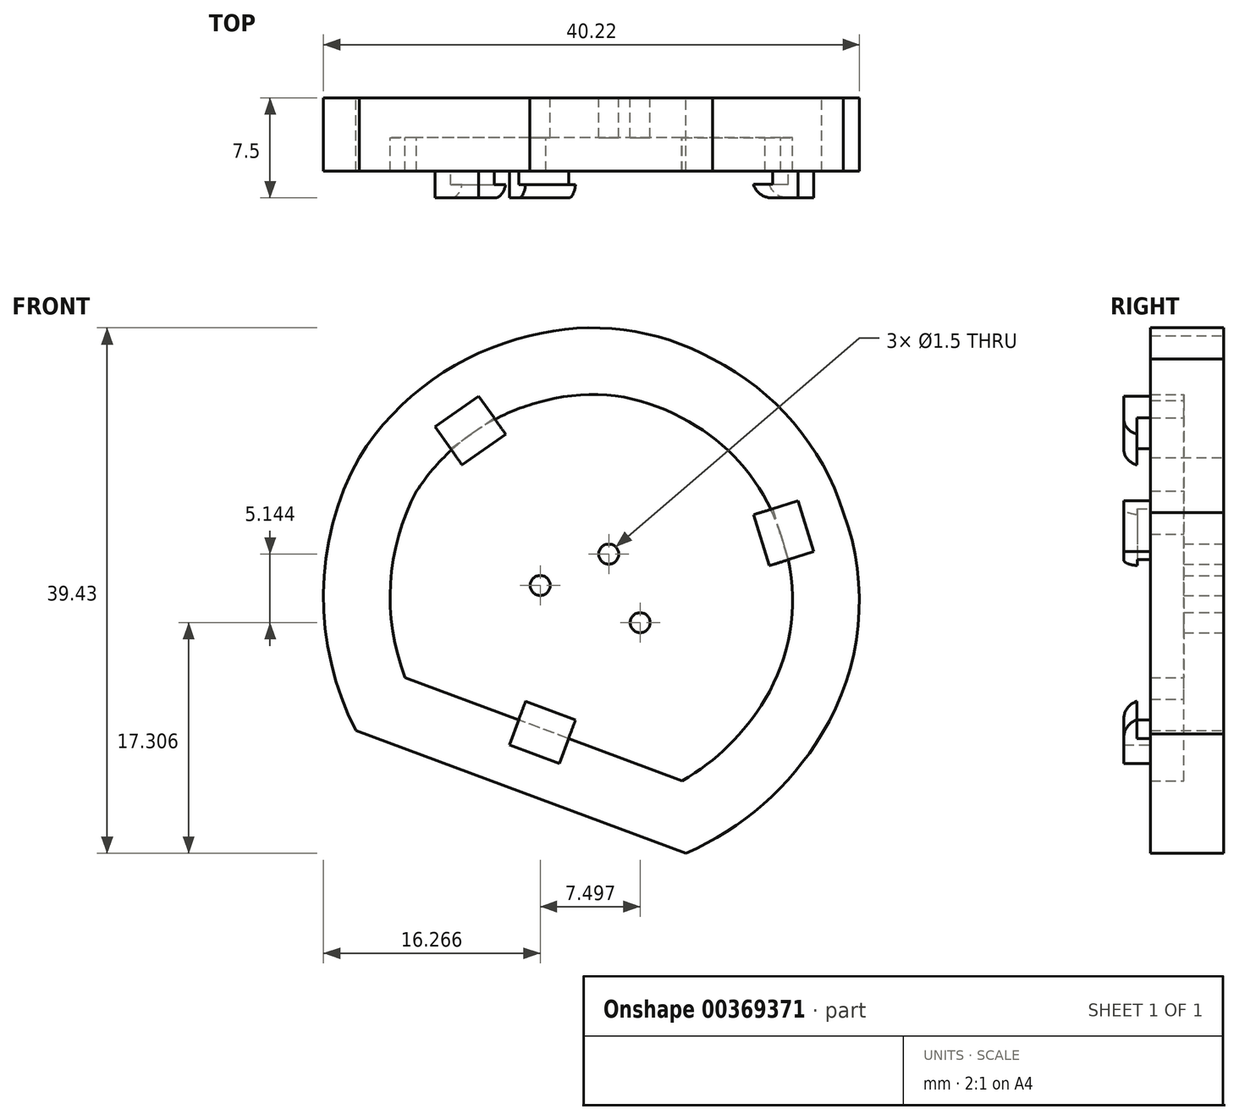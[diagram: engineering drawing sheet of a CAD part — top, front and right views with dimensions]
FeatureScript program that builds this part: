
annotation { "Feature Type Name" : "Feature", "Feature Type Description" : "" }
export const myFeature = defineFeature(function(context is Context, id is Id, definition is map)
    precondition{}
    {
        {
            var Q0;
            Q0=qCreatedBy(makeId("Front.planeOp"),FACE);
            var sketch = newSketch(context, id + "F0", { "sketchPlane" : qUnion([Q0])});
            skLineSegment(sketch, "E0", {"start": v(-81.78, 41.05) * mm, "end": v(-61, 33.31) * mm});
            skArc(sketch, "E1", {"start": v(-80.92, 55.04) * mm, "mid": v(-82.88, 48.14) * mm, "end": v(-81.78, 41.05) * mm});
            skArc(sketch, "E2", {"start": v(-71.22, 61.85) * mm, "mid": v(-76.74, 59.39) * mm, "end": v(-80.92, 55.04) * mm});
            skArc(sketch, "E3", {"start": v(-61.04, 60.54) * mm, "mid": v(-66, 62.19) * mm, "end": v(-71.22, 61.85) * mm});
            skArc(sketch, "E4", {"start": v(-53.61, 51.8) * mm, "mid": v(-56.44, 56.93) * mm, "end": v(-61.04, 60.54) * mm});
            skArc(sketch, "E5", {"start": v(-54.78, 39.42) * mm, "mid": v(-52.76, 45.48) * mm, "end": v(-53.61, 51.8) * mm});
            skArc(sketch, "E6", {"start": v(-61, 33.31) * mm, "mid": v(-57.5, 35.96) * mm, "end": v(-54.78, 39.42) * mm});
            skArc(sketch, "E7.0", {"start": v(-85.24, 57.58) * mm, "mid": v(-87.9, 47.36) * mm, "end": v(-85.48, 37.1) * mm});
            skArc(sketch, "E7.1", {"start": v(-72.42, 66.7) * mm, "mid": v(-79.72, 63.4) * mm, "end": v(-85.24, 57.58) * mm});
            skArc(sketch, "E7.2", {"start": v(-60.72, 27.87) * mm, "mid": v(-54.9, 31.55) * mm, "end": v(-50.5, 36.84) * mm});
            skArc(sketch, "E7.3", {"start": v(-50.5, 36.84) * mm, "mid": v(-47.78, 44.95) * mm, "end": v(-48.89, 53.44) * mm});
            skArc(sketch, "E7.4", {"start": v(-48.89, 53.44) * mm, "mid": v(-52.64, 60.18) * mm, "end": v(-58.7, 64.96) * mm});
            skLineSegment(sketch, "E7.5", {"start": v(-85.48, 37.1) * mm, "end": v(-60.72, 27.87) * mm});
            skArc(sketch, "E7.6", {"start": v(-58.7, 64.96) * mm, "mid": v(-65.4, 67.15) * mm, "end": v(-72.42, 66.7) * mm});
            skCircle(sketch, "E8", {"center": v(-66.5, 50.32) * mm, "radius": 0.75 * mm});
            skCircle(sketch, "E9", {"center": v(-71.64, 47.97) * mm, "radius": 0.75 * mm});
            skCircle(sketch, "E10", {"center": v(-64.15, 45.18) * mm, "radius": 0.75 * mm});
            skSolve(sketch);
        }
        {
            var Q0;
            Q0=makeQuery(id+"F0.imprint","IMPRINT",FACE,{"disambiguationData":[TD([[makeQuery(id+"F0.imprint","IMPRINT",EDGE,{"derivedFrom":sQuery(id+"F0.wireOp",EDGE,"E0")}),1.0]])]});
            var Q1;
            Q1=makeQuery(id+"F0.imprint","IMPRINT",FACE,{"disambiguationData":[TD([[makeQuery(id+"F0.imprint","IMPRINT",EDGE,{"derivedFrom":sQuery(id+"F0.wireOp",EDGE,"E0")}),-1.0]])]});
            extrude(context, id + "F1", {"entities" : qUnion([Q0, Q1]), "depth" : 3 * mm});
        }
        {
            var Q0;
            Q0 = qSketchRegion(id + "F0", true);
            extrude(context, id + "F2", {"entities" : qUnion([Q0]), "operationType" : NewBodyOperationType.ADD, "depth" : 5.5 * mm});
        }
        {
            var Q0;
            Q0=makeQuery(id+"F2.opExtrude","CAP_FACE",FACE,{"disambiguationData":[OSD([sQuery(id+"F0.wireOp",EDGE,"E0"),sQuery(id+"F0.wireOp",EDGE,"E1"),sQuery(id+"F0.wireOp",EDGE,"E2"),sQuery(id+"F0.wireOp",EDGE,"E3"),sQuery(id+"F0.wireOp",EDGE,"E4"),sQuery(id+"F0.wireOp",EDGE,"E5"),sQuery(id+"F0.wireOp",EDGE,"E6"),sQuery(id+"F0.wireOp",EDGE,"E7.0"),sQuery(id+"F0.wireOp",EDGE,"E7.1"),sQuery(id+"F0.wireOp",EDGE,"E7.2"),sQuery(id+"F0.wireOp",EDGE,"E7.3"),sQuery(id+"F0.wireOp",EDGE,"E7.4"),sQuery(id+"F0.wireOp",EDGE,"E7.5"),sQuery(id+"F0.wireOp",EDGE,"E7.6")])],"isStart":false});
            var sketch = newSketch(context, id + "F3", { "sketchPlane" : qUnion([Q0])});
            skLineSegment(sketch, "E11", {"start": v(-71.4, 37.18) * mm, "end": v(-73.26, 37.88) * mm});
            skLineSegment(sketch, "E12", {"start": v(-73.26, 37.88) * mm, "end": v(-73.96, 36) * mm});
            skLineSegment(sketch, "E13", {"start": v(-73.96, 36) * mm, "end": v(-70.21, 34.6) * mm});
            skLineSegment(sketch, "E14", {"start": v(-70.21, 34.6) * mm, "end": v(-69.52, 36.48) * mm});
            skLineSegment(sketch, "E15", {"start": v(-69.52, 36.48) * mm, "end": v(-71.4, 37.18) * mm});
            skSolve(sketch);
        }
        {
            var Q0;
            Q0 = qSketchRegion(id + "F3", true);
            extrude(context, id + "F4", {"entities" : qUnion([Q0]), "operationType" : NewBodyOperationType.ADD, "depth" : 2 * mm});
        }
        {
            var Q0;
            Q0=makeQuery(id+"F4.boolean.opBoolean","MERGE",FACE,{"derivedFrom":[makeQuery(id+"F2.opExtrude","SWEPT_FACE",FACE,{"disambiguationData":[OSD([sQuery(id+"F0.wireOp",EDGE,"E0")])]}),makeQuery(id+"F4.opExtrude","SWEPT_FACE",FACE,{"disambiguationData":[OSD([sQuery(id+"F3.wireOp",EDGE,"E11"),sQuery(id+"F3.wireOp",EDGE,"E15")])]})]});
            var sketch = newSketch(context, id + "F5", { "sketchPlane" : qUnion([Q0])});
            skLineSegment(sketch, "E16.bottom", {"start": v(-77.88, -7.5) * mm, "end": v(-81.88, -7.5) * mm});
            skLineSegment(sketch, "E16.top", {"start": v(-77.88, -6.5) * mm, "end": v(-81.88, -6.5) * mm});
            skLineSegment(sketch, "E16.left", {"start": v(-77.88, -7.5) * mm, "end": v(-77.88, -6.5) * mm});
            skLineSegment(sketch, "E16.right", {"start": v(-81.88, -7.5) * mm, "end": v(-81.88, -6.5) * mm});
            skSolve(sketch);
        }
        {
            var Q0;
            Q0 = qSketchRegion(id + "F5", true);
            extrude(context, id + "F6", {"entities" : qUnion([Q0]), "operationType" : NewBodyOperationType.ADD, "depth" : 1.5 * mm});
        }
        {
            var Q0;
            Q0=makeQuery(id+"F6.opExtrude","CAP_EDGE",EDGE,{"disambiguationData":[OSD([sQuery(id+"F5.wireOp",EDGE,"E16.bottom")])],"isStart":false});
            fillet(context, id + "F7", {"entities" : qUnion([Q0]), "radius" : 1.5 * mm, "tangentPropagation" : true, "allowEdgeOverflow" : false});
        }
        {
            var Q0;
            Q0=makeQuery(id+"F2.opExtrude","CAP_FACE",FACE,{"disambiguationData":[OSD([sQuery(id+"F0.wireOp",EDGE,"E0"),sQuery(id+"F0.wireOp",EDGE,"E1"),sQuery(id+"F0.wireOp",EDGE,"E2"),sQuery(id+"F0.wireOp",EDGE,"E3"),sQuery(id+"F0.wireOp",EDGE,"E4"),sQuery(id+"F0.wireOp",EDGE,"E5"),sQuery(id+"F0.wireOp",EDGE,"E6"),sQuery(id+"F0.wireOp",EDGE,"E7.0"),sQuery(id+"F0.wireOp",EDGE,"E7.1"),sQuery(id+"F0.wireOp",EDGE,"E7.2"),sQuery(id+"F0.wireOp",EDGE,"E7.3"),sQuery(id+"F0.wireOp",EDGE,"E7.4"),sQuery(id+"F0.wireOp",EDGE,"E7.5"),sQuery(id+"F0.wireOp",EDGE,"E7.6")])],"isStart":false});
            var sketch = newSketch(context, id + "F8", { "sketchPlane" : qUnion([Q0])});
            skLineSegment(sketch, "E17", {"start": v(-76.74, 59.39) * mm, "end": v(-75.1, 60.54) * mm});
            skLineSegment(sketch, "E18", {"start": v(-75.1, 60.54) * mm, "end": v(-76.25, 62.17) * mm});
            skLineSegment(sketch, "E19", {"start": v(-76.25, 62.17) * mm, "end": v(-79.53, 59.87) * mm});
            skLineSegment(sketch, "E20", {"start": v(-79.53, 59.87) * mm, "end": v(-78.38, 58.24) * mm});
            skLineSegment(sketch, "E21", {"start": v(-78.38, 58.24) * mm, "end": v(-76.74, 59.39) * mm});
            skLineSegment(sketch, "E22", {"start": v(-76.74, 59.39) * mm, "end": v(-53.61, 51.8) * mm});
            skLineSegment(sketch, "E23", {"start": v(-53.61, 51.8) * mm, "end": v(-54.21, 53.72) * mm});
            skLineSegment(sketch, "E24", {"start": v(-54.21, 53.72) * mm, "end": v(-52.3, 54.31) * mm});
            skLineSegment(sketch, "E25", {"start": v(-52.3, 54.31) * mm, "end": v(-51.11, 50.5) * mm});
            skLineSegment(sketch, "E26", {"start": v(-51.11, 50.5) * mm, "end": v(-53.02, 49.9) * mm});
            skLineSegment(sketch, "E27", {"start": v(-53.02, 49.9) * mm, "end": v(-53.61, 51.8) * mm});
            skSolve(sketch);
        }
        {
            var Q0;
            Q0 = qSketchRegion(id + "F8", true);
            extrude(context, id + "F9", {"entities" : qUnion([Q0]), "operationType" : NewBodyOperationType.ADD, "depth" : 2 * mm});
        }
        {
            var Q0;
            {var subQ0=sQuery(id+"F8.wireOp",EDGE,"E21");Q0=makeQuery(id+"F9.opExtrude","SWEPT_FACE",FACE,{"disambiguationData":[OSD([subQ0]),TDD([makeQuery(id+"F8.imprint","IMPRINT",EDGE,{"disambiguationData":[TD([[makeQuery(id+"F8.imprint","INTERSECT",VERTEX,{"derivedFrom":[sQuery(id+"F8.wireOp",EDGE,"E20"),subQ0]}),-1.0]])],"derivedFrom":subQ0})])]});}
            var sketch = newSketch(context, id + "F10", { "sketchPlane" : qUnion([Q0])});
            skLineSegment(sketch, "E28.bottom", {"start": v(-30.62, 7.5) * mm, "end": v(-26.62, 7.5) * mm});
            skLineSegment(sketch, "E28.top", {"start": v(-30.62, 6.5) * mm, "end": v(-26.62, 6.5) * mm});
            skLineSegment(sketch, "E28.left", {"start": v(-30.62, 7.5) * mm, "end": v(-30.62, 6.5) * mm});
            skLineSegment(sketch, "E28.right", {"start": v(-26.62, 7.5) * mm, "end": v(-26.62, 6.5) * mm});
            skSolve(sketch);
        }
        {
            var Q0;
            {var subQ0=sQuery(id+"F10.wireOp",EDGE,"E28.left");Q0=makeQuery(id+"F10.imprint","IMPRINT",FACE,{"disambiguationData":[TD([[makeQuery(id+"F10.imprint","IMPRINT",EDGE,{"derivedFrom":subQ0}),1.0]])]});}
            var Q1;
            {var subQ3=sQuery(id+"F10.wireOp",EDGE,"E28.right");Q1=makeQuery(id+"F10.imprint","IMPRINT",FACE,{"disambiguationData":[TD([[makeQuery(id+"F10.imprint","IMPRINT",EDGE,{"derivedFrom":subQ3}),-1.0]])]});}
            extrude(context, id + "F11", {"entities" : qUnion([Q0, Q1]), "operationType" : NewBodyOperationType.ADD, "depth" : 1.5 * mm});
        }
        {
            var Q0;
            Q0=makeQuery(id+"F11.opExtrude","CAP_EDGE",EDGE,{"disambiguationData":[OSD([sQuery(id+"F10.wireOp",EDGE,"E28.bottom")])],"isStart":false});
            fillet(context, id + "F12", {"entities" : qUnion([Q0]), "radius" : 1.5 * mm, "tangentPropagation" : true, "allowEdgeOverflow" : false});
        }
        {
            var Q0;
            Q0=makeQuery(id+"F9.opExtrude","SWEPT_FACE",FACE,{"disambiguationData":[OSD([sQuery(id+"F8.wireOp",EDGE,"E23")])]});
            var sketch = newSketch(context, id + "F13", { "sketchPlane" : qUnion([Q0])});
            skLineSegment(sketch, "E29.bottom", {"start": v(7.5, 67.44) * mm, "end": v(6.49, 67.44) * mm});
            skLineSegment(sketch, "E29.top", {"start": v(7.5, 63.44) * mm, "end": v(6.49, 63.44) * mm});
            skLineSegment(sketch, "E29.left", {"start": v(7.5, 67.44) * mm, "end": v(7.5, 63.44) * mm});
            skLineSegment(sketch, "E29.right", {"start": v(6.49, 67.44) * mm, "end": v(6.49, 63.44) * mm});
            skSolve(sketch);
        }
        {
            var Q0;
            {var subQ0=sQuery(id+"F13.wireOp",EDGE,"E29.bottom");Q0=makeQuery(id+"F13.imprint","IMPRINT",FACE,{"disambiguationData":[TD([[makeQuery(id+"F13.imprint","IMPRINT",EDGE,{"derivedFrom":subQ0}),1.0]])]});}
            var Q1;
            {var subQ0=sQuery(id+"F13.wireOp",EDGE,"E29.top");Q1=makeQuery(id+"F13.imprint","IMPRINT",FACE,{"disambiguationData":[TD([[makeQuery(id+"F13.imprint","IMPRINT",EDGE,{"derivedFrom":subQ0}),-1.0]])]});}
            extrude(context, id + "F14", {"entities" : qUnion([Q0, Q1]), "operationType" : NewBodyOperationType.ADD, "depth" : 1.5 * mm});
        }
        {
            var Q0;
            Q0=makeQuery(id+"F14.opExtrude","CAP_EDGE",EDGE,{"disambiguationData":[OSD([sQuery(id+"F13.wireOp",EDGE,"E29.left")])],"isStart":false});
            fillet(context, id + "F15", {"entities" : qUnion([Q0]), "radius" : 1.5 * mm, "tangentPropagation" : true, "allowEdgeOverflow" : false});
        }
    });
